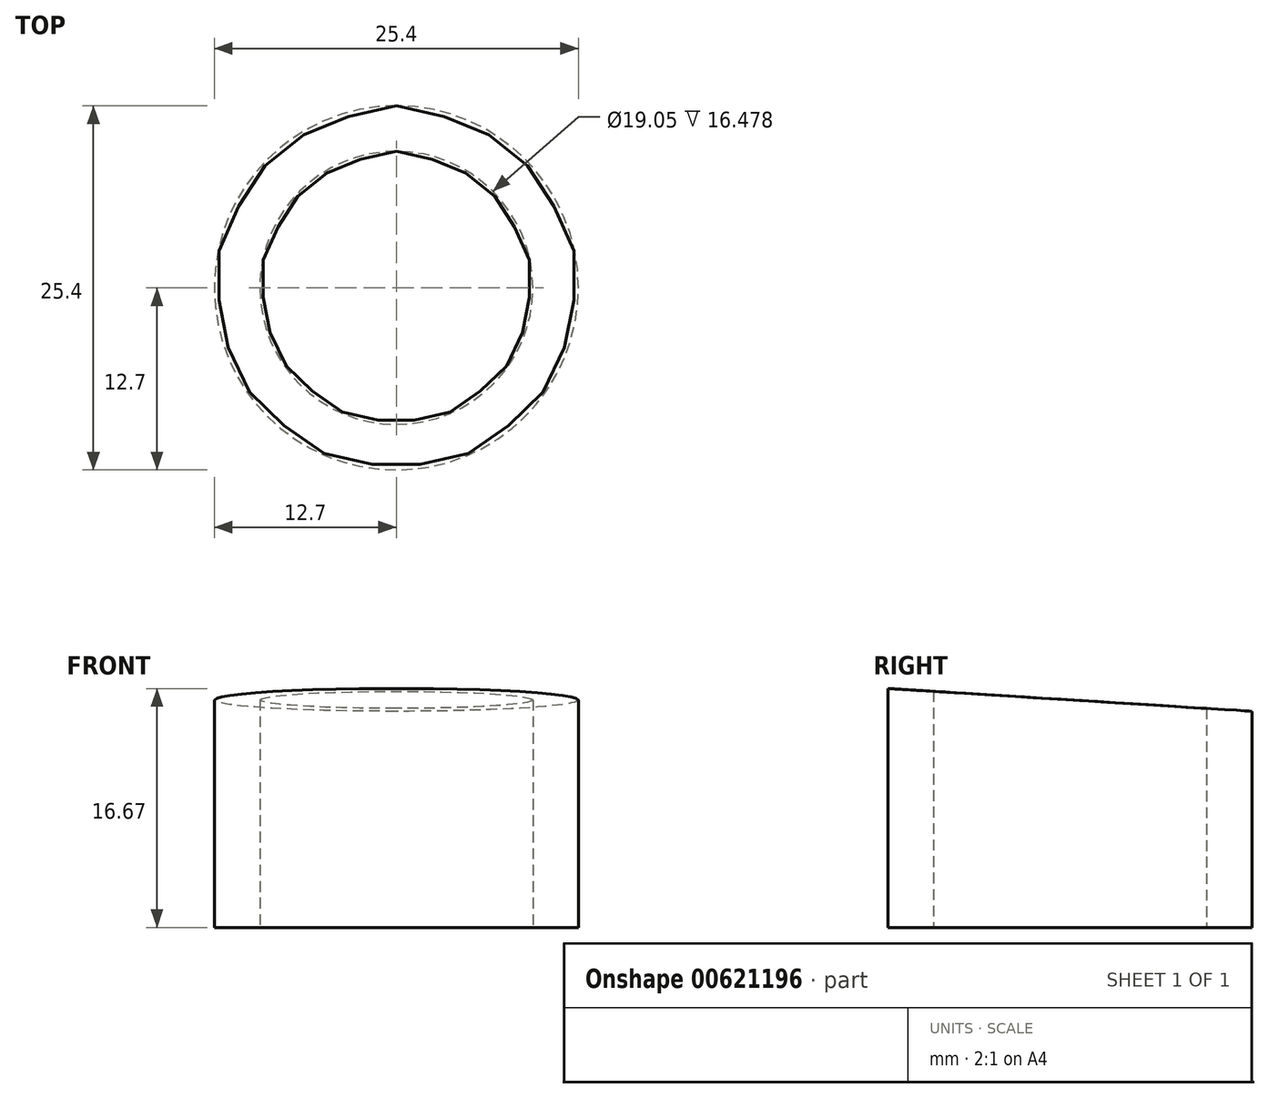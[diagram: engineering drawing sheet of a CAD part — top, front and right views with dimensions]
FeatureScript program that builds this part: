
annotation { "Feature Type Name" : "Feature", "Feature Type Description" : "" }
export const myFeature = defineFeature(function(context is Context, id is Id, definition is map)
    precondition{}
    {
        {
            var Q0;
            Q0=qCreatedBy(makeId("Top.planeOp"),FACE);
            var sketch = newSketch(context, id + "F0", { "sketchPlane" : qUnion([Q0])});
            skCircle(sketch, "E0", {"center": v(0, 0) * mm, "radius": 12.7 * mm});
            skCircle(sketch, "E1", {"center": v(0, 0) * mm, "radius": 9.53 * mm});
            skSolve(sketch);
        }
        {
            var Q0;
            Q0=makeQuery(id+"F0.imprint","IMPRINT",FACE,{"disambiguationData":[TD([[makeQuery(id+"F0.imprint","IMPRINT",EDGE,{"derivedFrom":sQuery(id+"F0.wireOp",EDGE,"E0")}),1.0]])]});
            extrude(context, id + "F1", {"entities" : qUnion([Q0]), "depth" : 50.8 * mm, "offsetDistance" : 25.4 * mm});
        }
        {
            var Q0;
            Q0=qCreatedBy(makeId("Right.planeOp"),FACE);
            var sketch = newSketch(context, id + "F2", { "sketchPlane" : qUnion([Q0])});
            skLineSegment(sketch, "E2", {"start": v(0, 0) * mm, "end": v(-50.8, 0) * mm});
            skLineSegment(sketch, "E3", {"start": v(-50.8, 0) * mm, "end": v(-50.8, 44.45) * mm});
            skLineSegment(sketch, "E4", {"start": v(-50.8, 44.45) * mm, "end": v(0, 41.28) * mm});
            skLineSegment(sketch, "E5", {"start": v(0, 0) * mm, "end": v(50.8, 0) * mm});
            skLineSegment(sketch, "E6", {"start": v(50.8, 0) * mm, "end": v(50.8, 38.1) * mm});
            skLineSegment(sketch, "E7", {"start": v(50.8, 38.1) * mm, "end": v(0, 41.28) * mm});
            skLineSegment(sketch, "E8", {"start": v(-50.8, 44.45) * mm, "end": v(-50.8, 59.3) * mm});
            skLineSegment(sketch, "E9", {"start": v(-50.8, 59.3) * mm, "end": v(50.8, 59.3) * mm});
            skLineSegment(sketch, "E10", {"start": v(50.8, 59.3) * mm, "end": v(50.8, 38.1) * mm});
            skLineSegment(sketch, "E11", {"start": v(0, 0) * mm, "end": v(0, 15.88) * mm});
            skLineSegment(sketch, "E12", {"start": v(0, 15.88) * mm, "end": v(-50.8, 19.05) * mm});
            skLineSegment(sketch, "E13", {"start": v(-50.8, 19.05) * mm, "end": v(50.8, 12.7) * mm});
            skSolve(sketch);
        }
        {
            var Q0;
            Q0=makeQuery(id+"F2.imprint","IMPRINT",FACE,{"disambiguationData":[TD([[makeQuery(id+"F2.imprint","IMPRINT",EDGE,{"derivedFrom":sQuery(id+"F2.wireOp",EDGE,"E4")}),1.0]])]});
            var Q1;
            {var subQ4=sQuery(id+"F2.wireOp",EDGE,"E4");Q1=makeQuery(id+"F2.imprint","IMPRINT",FACE,{"disambiguationData":[TD([[makeQuery(id+"F2.imprint","IMPRINT",EDGE,{"derivedFrom":subQ4}),-1.0]])]});}
            var Q2;
            Q2=makeQuery(id+"F1.opExtrude","SWEPT_FACE",FACE,{"disambiguationData":[OSD([sQuery(id+"F0.wireOp",EDGE,"E0")])]});
            extrude(context, id + "F3", {"entities" : qUnion([Q0, Q1]), "operationType" : NewBodyOperationType.REMOVE, "endBound" : BoundingType.SYMMETRIC, "depth" : 25.4 * mm, "endBoundEntityFace" : qUnion([Q2]), "offsetDistance" : 25.4 * mm});
        }
    });
